# Revit family: Construction_Stairs-Precision_Ladders-Fixed_Ladder-V1
name_source: partatom
category: Specialty Equipment
units: mm (PartAtom-declared; Revit-internal decimal feet)

## family parameters
Cut with Voids When Loaded = No
Host = Face
OmniClass Number = 23.30.70.17.14
OmniClass Title = Vertical Ladders
Part Type = Normal
Room Calculation Point = No
Round Connector Dimension = Use Diameter
Shared = No

## types (3) — shared parameters
Caps Material = Plastic -Precision Ladders LLC - Polyurethane - Black
Default Elevation = 0"
Description = Vertical wall ladder for rooftop access or roof hatch access
Manufacturer = Precision Ladders, LLC
Material = Metal - Precision Ladders LLC - Aluminum - Mill Finish
Model = Fixed Aluminum Wall Ladders
Product Page URL = https://precisionladders.com
Product data url = https://www.bimobject.com
Riser Height = 12"
URL = http://www.precisionladders.com

## per-type parameters (varying)
| type | Cap | Model Number |
| With Overshoot | No | FL-04 |
| To Roof Hatch | Yes | FL-02 |
| With Walk-Thru | Yes | FL-05 |

type visibility flags: 3 boolean params named "<type name>" — each type sets only its own to Yes (folded from table)

## geometry (parser evidence)
native form markers: Blend x8, Sweep x7
no freeform markers — native parametric forms only
